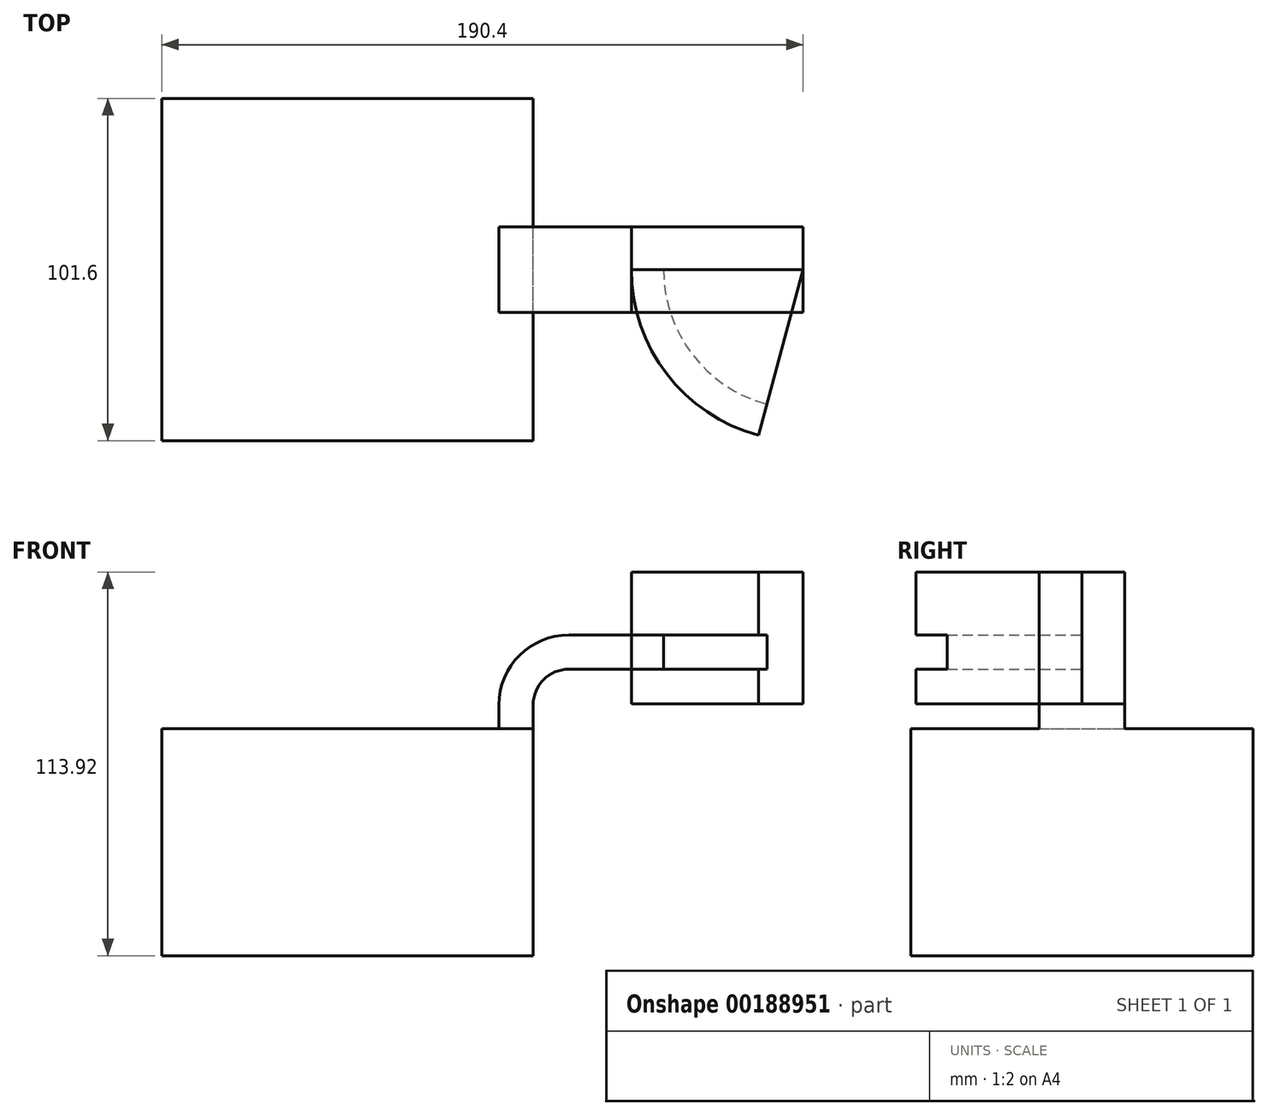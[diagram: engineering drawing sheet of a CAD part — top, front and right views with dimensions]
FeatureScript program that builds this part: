
annotation { "Feature Type Name" : "Feature", "Feature Type Description" : "" }
export const myFeature = defineFeature(function(context is Context, id is Id, definition is map)
    precondition{}
    {
        {
            var Q0;
            Q0=qCreatedBy(makeId("Front.planeOp"),FACE);
            var sketch = newSketch(context, id + "F0", { "sketchPlane" : qUnion([Q0])});
            skLineSegment(sketch, "E0.bottom", {"start": v(-55.13, 33.7) * mm, "end": v(55.13, 33.7) * mm});
            skLineSegment(sketch, "E0.top", {"start": v(-55.13, -33.7) * mm, "end": v(55.13, -33.7) * mm});
            skLineSegment(sketch, "E0.left", {"start": v(-55.13, 33.7) * mm, "end": v(-55.13, -33.7) * mm});
            skLineSegment(sketch, "E0.right", {"start": v(55.13, 33.7) * mm, "end": v(55.13, -33.7) * mm});
            skPoint(sketch, "E0.middle", {"position": v(0, 0) * mm});
            skLineSegment(sketch, "E1.bottom", {"start": v(135.27, 41.08) * mm, "end": v(84.28, 41.08) * mm});
            skLineSegment(sketch, "E1.top", {"start": v(135.27, 80.22) * mm, "end": v(84.28, 80.22) * mm});
            skLineSegment(sketch, "E1.left", {"start": v(135.27, 41.08) * mm, "end": v(135.27, 80.22) * mm});
            skLineSegment(sketch, "E1.right", {"start": v(84.28, 41.08) * mm, "end": v(84.28, 80.22) * mm});
            skPoint(sketch, "E1.middle", {"position": v(109.77, 60.65) * mm});
            skLineSegment(sketch, "E2", {"start": v(55.13, 33.7) * mm, "end": v(55.13, 40.75) * mm});
            skArc(sketch, "E3", {"start": v(55.13, 40.75) * mm, "mid": v(58.24, 48.25) * mm, "end": v(65.73, 51.35) * mm});
            skLineSegment(sketch, "E4", {"start": v(65.73, 51.35) * mm, "end": v(93.84, 51.35) * mm});
            skLineSegment(sketch, "E5.0", {"start": v(65.73, 61.51) * mm, "end": v(93.84, 61.51) * mm});
            skArc(sketch, "E5.1", {"start": v(44.97, 40.75) * mm, "mid": v(51.05, 55.43) * mm, "end": v(65.73, 61.51) * mm});
            skLineSegment(sketch, "E5.2", {"start": v(44.97, 24.43) * mm, "end": v(44.97, 40.75) * mm});
            skLineSegment(sketch, "E6", {"start": v(93.84, 51.35) * mm, "end": v(93.84, 61.51) * mm});
            skFitSpline(sketch, "E7", {"points": [v(-55.13, 33.7) * mm, v(84.28, 61.51) * mm], "startDerivative": vector(29.28, 139.56) * mm, "endDerivative": vector(0, -56.11) * mm});
            skSolve(sketch);
        }
        {
            var Q0;
            Q0=makeQuery(id+"F0.imprint","IMPRINT",FACE,{"disambiguationData":[TD([[makeQuery(id+"F0.imprint","IMPRINT",EDGE,{"derivedFrom":sQuery(id+"F0.wireOp",EDGE,"E0.top")}),1.0]])]});
            extrude(context, id + "F1", {"entities" : qUnion([Q0]), "endBound" : BoundingType.SYMMETRIC, "depth" : 101.6 * mm});
        }
        {
            var Q0;
            {var subQ1=sQuery(id+"F0.wireOp",EDGE,"E1.bottom");Q0=makeQuery(id+"F0.imprint","IMPRINT",FACE,{"disambiguationData":[TD([[makeQuery(id+"F0.imprint","IMPRINT",EDGE,{"derivedFrom":subQ1}),-1.0]])]});}
            var Q1;
            {var subQ1=sQuery(id+"F0.wireOp",EDGE,"E2");Q1=makeQuery(id+"F0.imprint","IMPRINT",FACE,{"disambiguationData":[TD([[makeQuery(id+"F0.imprint","IMPRINT",EDGE,{"derivedFrom":subQ1}),1.0]])]});}
            var Q2;
            {var subQ0=sQuery(id+"F0.wireOp",EDGE,"E5.1");Q2=makeQuery(id+"F0.imprint","IMPRINT",FACE,{"disambiguationData":[TD([[makeQuery(id+"F0.imprint","IMPRINT",EDGE,{"derivedFrom":subQ0}),1.0]])]});}
            extrude(context, id + "F2", {"entities" : qUnion([Q0, Q1, Q2]), "operationType" : NewBodyOperationType.ADD, "endBound" : BoundingType.SYMMETRIC, "depth" : 25.4 * mm});
        }
        {
            var Q0;
            {var subQ1=sQuery(id+"F0.wireOp",EDGE,"E1.bottom");Q0=makeQuery(id+"F0.imprint","IMPRINT",FACE,{"disambiguationData":[TD([[makeQuery(id+"F0.imprint","IMPRINT",EDGE,{"derivedFrom":subQ1}),-1.0]])]});}
            var Q1;
            Q1=sQuery(id+"F0.wireOp",EDGE,"E1.left");
            revolve(context, id + "F3", {"entities" : qUnion([Q0]), "axis" : qUnion([Q1]), "revolveType" : RevolveType.ONE_DIRECTION, "angle" : 75 * degree});
        }
    });
